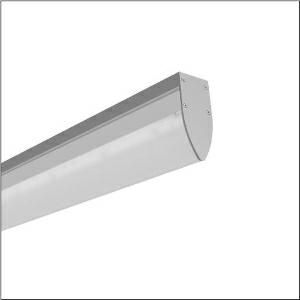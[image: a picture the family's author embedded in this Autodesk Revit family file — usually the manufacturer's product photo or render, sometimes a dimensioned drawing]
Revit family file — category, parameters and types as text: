
# Revit family: mira_21_td_51fr527k474a
name_source: partatom
category: Lighting Fixtures
units: mm (PartAtom-declared; Revit-internal decimal feet)

## family parameters
Cut with Voids When Loaded = No
Host = Face
Light Source = No
Part Type = Normal
Room Calculation Point = No
Round Connector Dimension = Use Diameter
Shared = No

## types (1)
- Mira 21 TD (1 x LED, 7330 lm, 52 W, 4000K)
    Apparent Load = 52 VA
    CIE Flux Codes = 40 68 87 81 100
    Color Rendering = 80
    Color Temperature = 4000K
    Default Elevation = 1800 mm
    Description = Mira 21 TD, clean room luminaire, primary light control with reflector, primary optical cover: cover, of PMMA, frosted, light emission: direct distribution, primary light characteristic: symmetric, installation type: surface-mounted, LED, rated luminous flux: 7.330lm, luminous efficacy: 141lm/W, light colour: 840, colour temperature: 4000K, control gear: ON/OFF, with terminal, 3-pole, max. 2.5mm², mains connection: 230V, AC, 50/60Hz, rated input power: 52W, luminaire housing, of sheet steel, coated, pure white (RAL 9010), length: 1.200mm, width: 55mm, height: 120mm, protection rating (complete): IP43, insulation class (complete): insulation class I (protective earthing), certification: CE, UKCA, permissible operating ambient temperature: -5..+40°C, standard: EN 50419, packaging unit: 1 piece
    Height = 120 mm
    Lamp = 1 x LED
    Lamp Light Flux = 7330 lm
    Lamp Power = 52 W
    Lamp count = 1
    Length = 1200 mm
    Luminous efficacy = 141 lm/W
    Manufacturer = Siteco
    ModVariant = No
    Model = 51FR527K474A
    Mounting Place = Ceiling
    Mounting Type = Surface mounted
    Number of Poles = 1
    OnlyDefault = Yes
    Power Factor = 1
    Product Name = Mira 21 TD
    Product group = clean room luminaire | ceiling mounted
    ProductGroupID = 306
    Protection Class = Protection class I
    Protection Degree = IP 43
    RLX_Detail_Level = 1
    RLX_Emergency_Light_Flux = 0 lm
    RLX_Emergency_Type = 0
    RLX_Emergency_Type_DB = No
    RlxData = <blob elided: 25161 chars, md5=fdc47ebf>
    Socket = socket
    Standby Power = 0 W
    System Light Flux = 7330 lm
    System Power = 52 W
    Type Comments = Product without accessories
    Type Image = l_1007115.jpg
    URL = http://relux.com
    VarID = ---
    Voltage = 0 V
    Weight = 0.00 kg
    Width = 55 mm

## geometry (parser evidence)
native form markers: Blend x4, Sweep x13
no freeform markers — native parametric forms only
